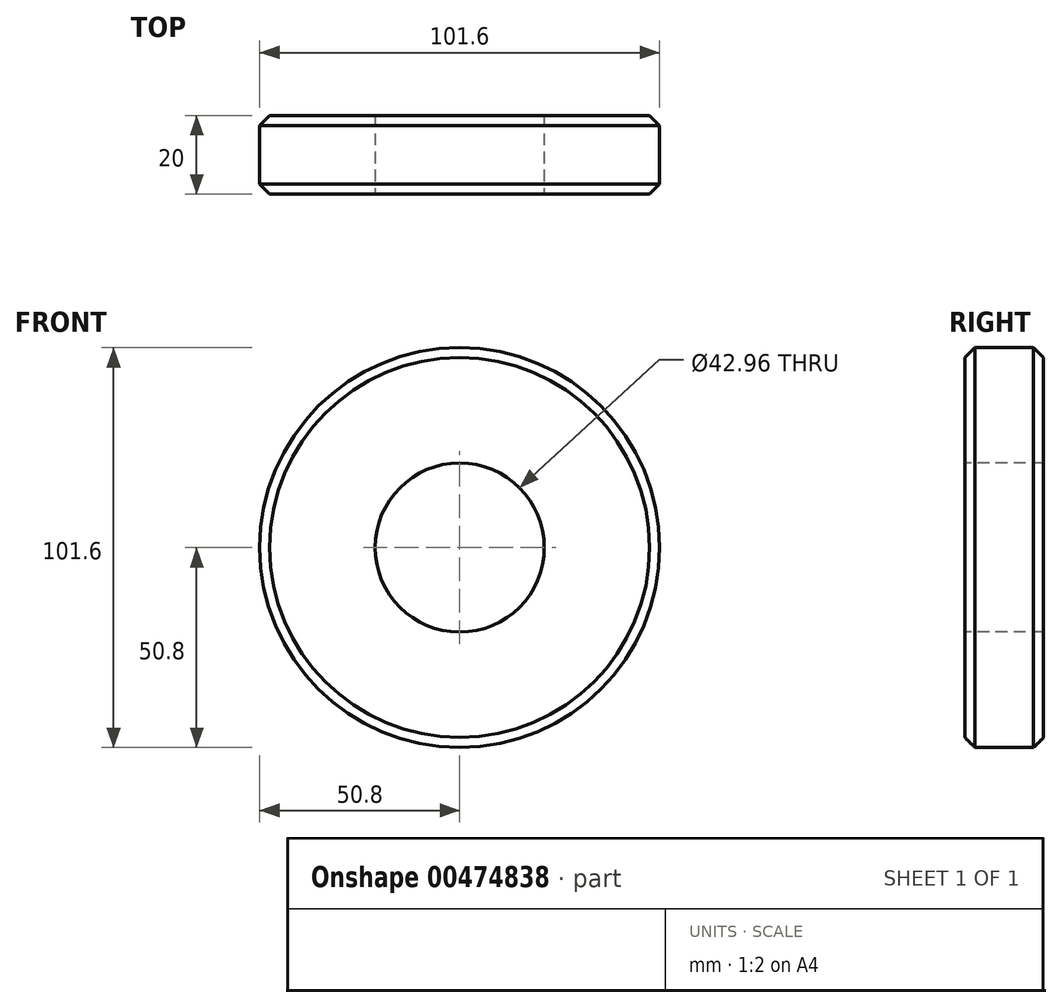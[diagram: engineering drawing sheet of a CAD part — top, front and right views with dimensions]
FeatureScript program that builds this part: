
annotation { "Feature Type Name" : "Feature", "Feature Type Description" : "" }
export const myFeature = defineFeature(function(context is Context, id is Id, definition is map)
    precondition{}
    {
        {
            var Q0;
            Q0=qCreatedBy(makeId("Front.planeOp"),FACE);
            var sketch = newSketch(context, id + "F0", { "sketchPlane" : qUnion([Q0])});
            skCircle(sketch, "E0", {"center": v(0, 0) * mm, "radius": 50.8 * mm});
            skSolve(sketch);
        }
        {
            var Q0;
            Q0=makeQuery(id+"F0.imprint","IMPRINT",FACE,{"disambiguationData":[TD([[makeQuery(id+"F0.imprint","IMPRINT",EDGE,{"derivedFrom":sQuery(id+"F0.wireOp",EDGE,"E0")}),1.0]])]});
            extrude(context, id + "F1", {"entities" : qUnion([Q0]), "depth" : 20 * mm});
        }
        {
            var Q0;
            Q0=makeQuery(id+"F1.opExtrude","CAP_FACE",FACE,{"disambiguationData":[OSD([sQuery(id+"F0.wireOp",EDGE,"E0")])],"isStart":false});
            var sketch = newSketch(context, id + "F2", { "sketchPlane" : qUnion([Q0])});
            skCircle(sketch, "E1", {"center": v(0, 0) * mm, "radius": 21.48 * mm});
            skSolve(sketch);
        }
        {
            var Q0;
            Q0=makeQuery(id+"F1.opExtrude","CAP_EDGE",EDGE,{"disambiguationData":[OSD([sQuery(id+"F0.wireOp",EDGE,"E0")])],"isStart":false});
            var Q1;
            Q1=makeQuery(id+"F1.opExtrude","CAP_EDGE",EDGE,{"disambiguationData":[OSD([sQuery(id+"F0.wireOp",EDGE,"E0")])],"isStart":true});
            chamfer(context, id + "F3", {"entities" : qUnion([Q0, Q1]), "width" : 2.54 * mm, "tangentPropagation" : true});
        }
        {
            var Q0;
            Q0=makeQuery(id+"F2.imprint","IMPRINT",FACE,{"disambiguationData":[TD([[makeQuery(id+"F2.imprint","IMPRINT",EDGE,{"derivedFrom":sQuery(id+"F2.wireOp",EDGE,"E1")}),1.0]])]});
            extrude(context, id + "F4", {"entities" : qUnion([Q0]), "operationType" : NewBodyOperationType.REMOVE, "endBound" : BoundingType.UP_TO_NEXT, "oppositeDirection" : true, "depth" : 25.4 * mm});
        }
    });
